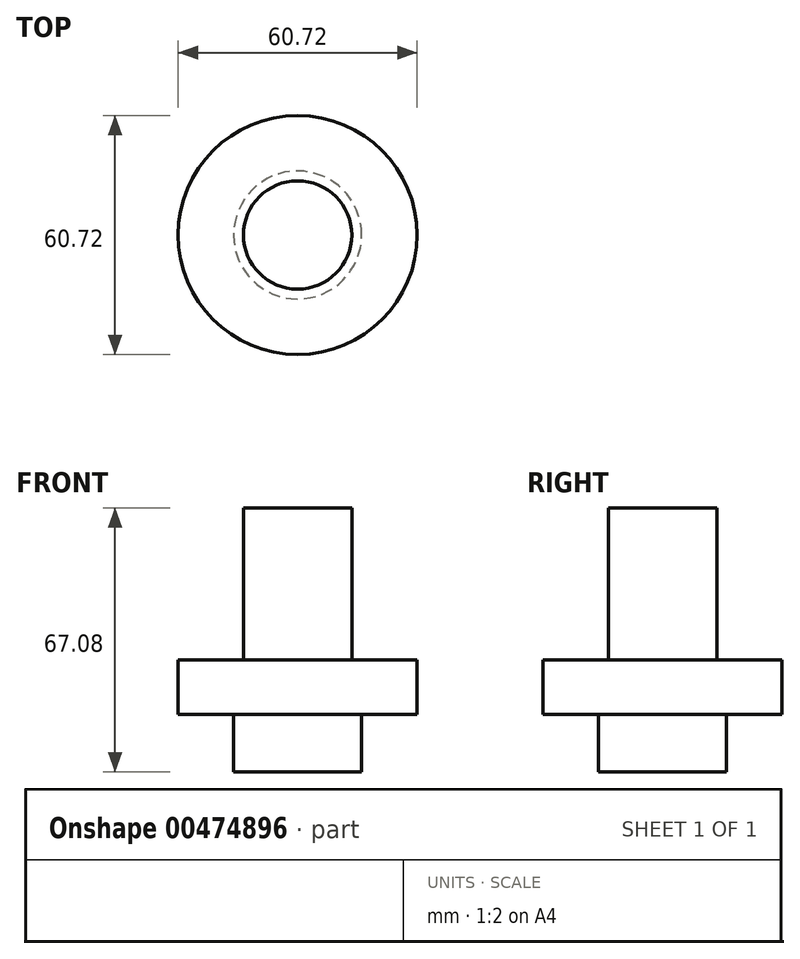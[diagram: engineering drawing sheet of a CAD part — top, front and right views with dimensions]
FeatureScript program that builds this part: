
annotation { "Feature Type Name" : "Feature", "Feature Type Description" : "" }
export const myFeature = defineFeature(function(context is Context, id is Id, definition is map)
    precondition{}
    {
        {
            var Q0;
            Q0=qCreatedBy(makeId("Front.planeOp"),FACE);
            var sketch = newSketch(context, id + "F0", { "sketchPlane" : qUnion([Q0])});
            skLineSegment(sketch, "E0", {"start": v(0, -28.49) * mm, "end": v(-16.26, -28.49) * mm});
            skLineSegment(sketch, "E1", {"start": v(-16.26, -28.49) * mm, "end": v(-16.26, -13.9) * mm});
            skLineSegment(sketch, "E2", {"start": v(-16.26, -13.9) * mm, "end": v(-30.36, -13.9) * mm});
            skLineSegment(sketch, "E3", {"start": v(-30.36, -13.9) * mm, "end": v(-30.36, 0) * mm});
            skLineSegment(sketch, "E4", {"start": v(-30.36, 0) * mm, "end": v(-13.76, 0) * mm});
            skLineSegment(sketch, "E5", {"start": v(-13.76, 0) * mm, "end": v(-13.76, 38.59) * mm});
            skLineSegment(sketch, "E6", {"start": v(-13.76, 38.59) * mm, "end": v(0, 38.59) * mm});
            skLineSegment(sketch, "E7", {"start": v(0, 38.59) * mm, "end": v(0, -28.49) * mm});
            skSolve(sketch);
        }
        {
            var Q0;
            Q0=makeQuery(id+"F0.imprint","IMPRINT",FACE,{"disambiguationData":[TD([[makeQuery(id+"F0.imprint","IMPRINT",EDGE,{"derivedFrom":sQuery(id+"F0.wireOp",EDGE,"E0")}),-1.0]])]});
            var Q1;
            Q1=sQuery(id+"F0.wireOp",EDGE,"E7");
            revolve(context, id + "F1", {"entities" : qUnion([Q0]), "axis" : qUnion([Q1]), "revolveType" : RevolveType.FULL});
        }
    });
